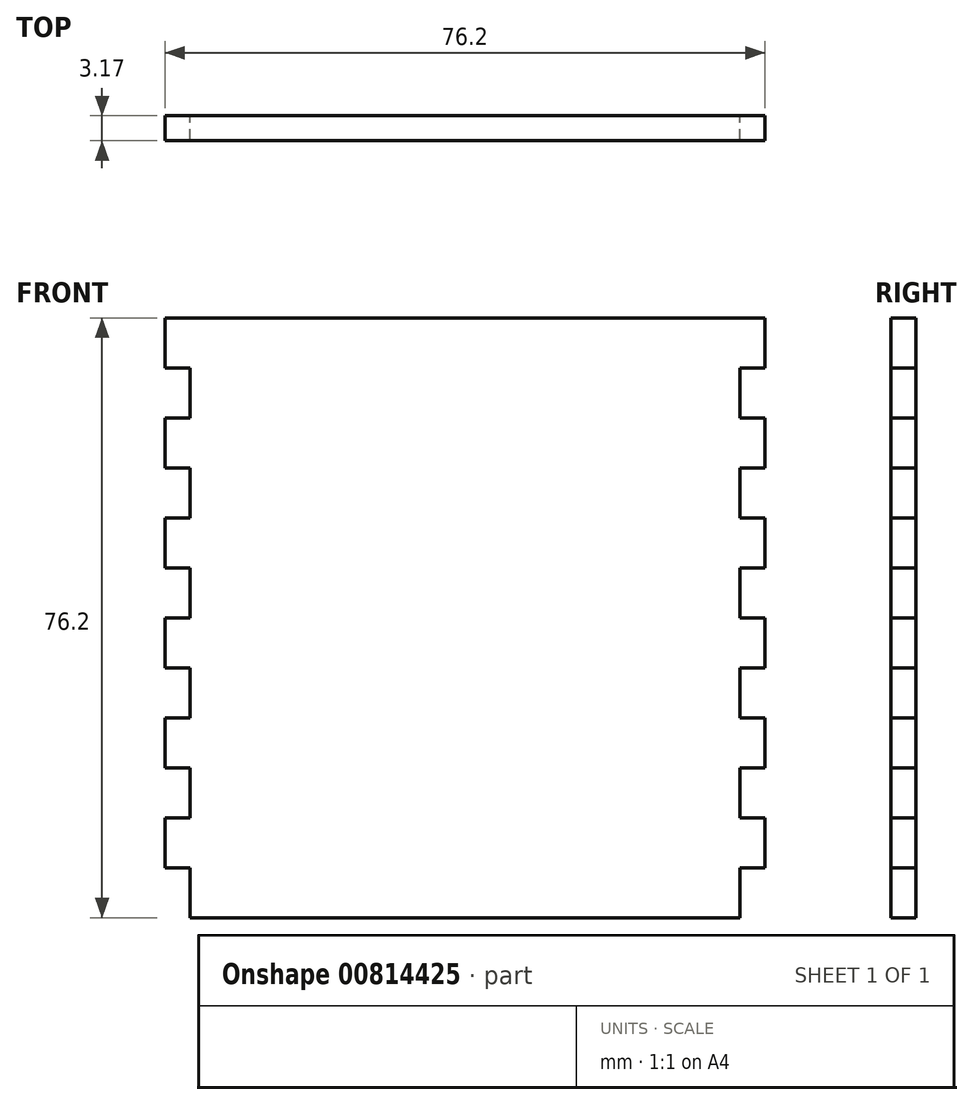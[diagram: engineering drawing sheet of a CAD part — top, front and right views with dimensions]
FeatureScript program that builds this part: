
annotation { "Feature Type Name" : "Feature", "Feature Type Description" : "" }
export const myFeature = defineFeature(function(context is Context, id is Id, definition is map)
    precondition{}
    {
        {
            var Q0;
            Q0=qCreatedBy(makeId("Front.planeOp"),FACE);
            var sketch = newSketch(context, id + "F0", { "sketchPlane" : qUnion([Q0])});
            skLineSegment(sketch, "E0.bottom", {"start": v(-38.1, 38.1) * mm, "end": v(38.1, 38.1) * mm});
            skLineSegment(sketch, "E0.top", {"start": v(-38.1, -38.1) * mm, "end": v(38.1, -38.1) * mm});
            skLineSegment(sketch, "E0.left", {"start": v(-38.1, 38.1) * mm, "end": v(-38.1, -38.1) * mm});
            skLineSegment(sketch, "E0.right", {"start": v(38.1, 38.1) * mm, "end": v(38.1, -38.1) * mm});
            skLineSegment(sketch, "E1", {"start": v(38.1, 31.75) * mm, "end": v(34.92, 31.75) * mm});
            skLineSegment(sketch, "E2", {"start": v(34.92, 31.75) * mm, "end": v(34.92, 25.4) * mm});
            skLineSegment(sketch, "E3", {"start": v(34.92, 25.4) * mm, "end": v(38.1, 25.4) * mm});
            skLineSegment(sketch, "E4.bottom", {"start": v(38.1, 19.05) * mm, "end": v(34.92, 19.05) * mm});
            skLineSegment(sketch, "E4.top", {"start": v(38.1, 12.7) * mm, "end": v(34.92, 12.7) * mm});
            skLineSegment(sketch, "E4.left", {"start": v(38.1, 19.05) * mm, "end": v(38.1, 12.7) * mm});
            skLineSegment(sketch, "E4.right", {"start": v(34.92, 19.05) * mm, "end": v(34.92, 12.7) * mm});
            skLineSegment(sketch, "E5.bottom", {"start": v(38.1, 6.35) * mm, "end": v(34.92, 6.35) * mm});
            skLineSegment(sketch, "E5.top", {"start": v(38.1, 0) * mm, "end": v(34.92, 0) * mm});
            skLineSegment(sketch, "E5.left", {"start": v(38.1, 6.35) * mm, "end": v(38.1, 0) * mm});
            skLineSegment(sketch, "E5.right", {"start": v(34.92, 6.35) * mm, "end": v(34.92, 0) * mm});
            skLineSegment(sketch, "E6.bottom", {"start": v(38.1, -6.35) * mm, "end": v(34.93, -6.35) * mm});
            skLineSegment(sketch, "E6.top", {"start": v(38.1, -12.7) * mm, "end": v(34.93, -12.7) * mm});
            skLineSegment(sketch, "E6.left", {"start": v(38.1, -6.35) * mm, "end": v(38.1, -12.7) * mm});
            skLineSegment(sketch, "E6.right", {"start": v(34.93, -6.35) * mm, "end": v(34.93, -12.7) * mm});
            skLineSegment(sketch, "E7.bottom", {"start": v(38.1, -19.05) * mm, "end": v(34.93, -19.05) * mm});
            skLineSegment(sketch, "E7.top", {"start": v(38.1, -25.4) * mm, "end": v(34.93, -25.4) * mm});
            skLineSegment(sketch, "E7.left", {"start": v(38.1, -19.05) * mm, "end": v(38.1, -25.4) * mm});
            skLineSegment(sketch, "E7.right", {"start": v(34.93, -19.05) * mm, "end": v(34.93, -25.4) * mm});
            skLineSegment(sketch, "E8.bottom", {"start": v(38.1, -31.75) * mm, "end": v(34.93, -31.75) * mm});
            skLineSegment(sketch, "E8.top", {"start": v(38.1, -38.1) * mm, "end": v(34.93, -38.1) * mm});
            skLineSegment(sketch, "E8.left", {"start": v(38.1, -31.75) * mm, "end": v(38.1, -38.1) * mm});
            skLineSegment(sketch, "E8.right", {"start": v(34.93, -31.75) * mm, "end": v(34.93, -38.1) * mm});
            skLineSegment(sketch, "E9.MirrorCS", {"start": v(-38.1, -12.7) * mm, "end": v(-34.93, -12.7) * mm});
            skLineSegment(sketch, "E10.MirrorCS", {"start": v(-38.1, -25.4) * mm, "end": v(-34.93, -25.4) * mm});
            skLineSegment(sketch, "E11.MirrorCS", {"start": v(-38.1, -31.75) * mm, "end": v(-34.93, -31.75) * mm});
            skLineSegment(sketch, "E12.MirrorCS", {"start": v(-38.1, -38.1) * mm, "end": v(-34.93, -38.1) * mm});
            skLineSegment(sketch, "E13.MirrorCS", {"start": v(-38.1, -19.05) * mm, "end": v(-34.93, -19.05) * mm});
            skLineSegment(sketch, "E14.MirrorCS", {"start": v(-38.1, 0) * mm, "end": v(-34.92, 0) * mm});
            skLineSegment(sketch, "E15.MirrorCS", {"start": v(-38.1, 6.35) * mm, "end": v(-34.92, 6.35) * mm});
            skLineSegment(sketch, "E16.MirrorCS", {"start": v(-38.1, 12.7) * mm, "end": v(-34.92, 12.7) * mm});
            skLineSegment(sketch, "E17.MirrorCS", {"start": v(-38.1, -6.35) * mm, "end": v(-34.93, -6.35) * mm});
            skLineSegment(sketch, "E18.MirrorCS", {"start": v(-38.1, 19.05) * mm, "end": v(-34.92, 19.05) * mm});
            skLineSegment(sketch, "E19.MirrorCS", {"start": v(-38.1, -19.05) * mm, "end": v(-38.1, -25.4) * mm});
            skLineSegment(sketch, "E20.MirrorCS", {"start": v(-38.1, -6.35) * mm, "end": v(-38.1, -12.7) * mm});
            skLineSegment(sketch, "E21.MirrorCS", {"start": v(-38.1, 6.35) * mm, "end": v(-38.1, 0) * mm});
            skLineSegment(sketch, "E22.MirrorCS", {"start": v(-34.92, 25.4) * mm, "end": v(-38.1, 25.4) * mm});
            skLineSegment(sketch, "E23.MirrorCS", {"start": v(-38.1, 31.75) * mm, "end": v(-34.92, 31.75) * mm});
            skLineSegment(sketch, "E24.MirrorCS", {"start": v(-34.93, -31.75) * mm, "end": v(-34.93, -38.1) * mm});
            skLineSegment(sketch, "E25.MirrorCS", {"start": v(-34.93, -6.35) * mm, "end": v(-34.93, -12.7) * mm});
            skLineSegment(sketch, "E26.MirrorCS", {"start": v(-34.93, -19.05) * mm, "end": v(-34.93, -25.4) * mm});
            skLineSegment(sketch, "E27.MirrorCS", {"start": v(-38.1, -31.75) * mm, "end": v(-38.1, -38.1) * mm});
            skLineSegment(sketch, "E28.MirrorCS", {"start": v(-34.92, 6.35) * mm, "end": v(-34.92, 0) * mm});
            skLineSegment(sketch, "E29.MirrorCS", {"start": v(-34.92, 19.05) * mm, "end": v(-34.92, 12.7) * mm});
            skLineSegment(sketch, "E30.MirrorCS", {"start": v(-38.1, 19.05) * mm, "end": v(-38.1, 12.7) * mm});
            skLineSegment(sketch, "E31.MirrorCS", {"start": v(-34.92, 31.75) * mm, "end": v(-34.92, 25.4) * mm});
            skSolve(sketch);
        }
        {
            var Q0;
            {var subQ1=sQuery(id+"F0.wireOp",EDGE,"E0.bottom");Q0=makeQuery(id+"F0.imprint","IMPRINT",FACE,{"disambiguationData":[TD([[makeQuery(id+"F0.imprint","IMPRINT",EDGE,{"derivedFrom":subQ1}),-1.0]])]});}
            extrude(context, id + "F1", {"entities" : qUnion([Q0]), "depth" : 3.17 * mm, "offsetDistance" : 25.4 * mm});
        }
    });
